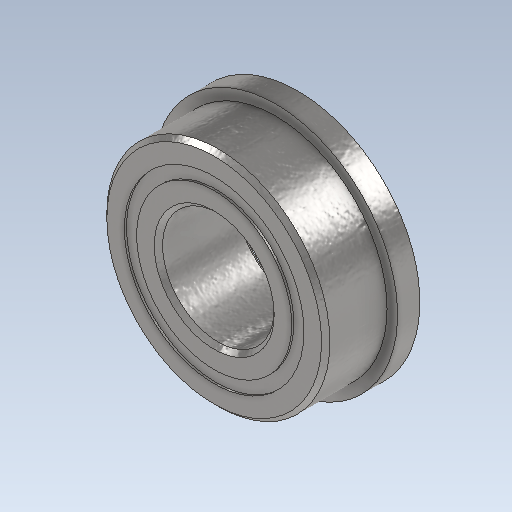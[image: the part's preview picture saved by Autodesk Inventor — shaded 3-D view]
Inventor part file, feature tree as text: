
AUTODESK INVENTOR PART (.ipt)
format: ipt  version: 2023 (Build 270158000, 158)  size: 664,576 bytes
history: native  units: in
note: dims shown in document units (in); Inventor stores cm internally (conversion verified against a paired STEP export)
features: other x11, revolve x5
ambient origin geometry x8: Origin, YZ Plane, XZ Plane, XY Plane, X Axis, Y Axis, Z Axis, Center Point
bodies: Solid1 (feature_tree), Solid2 (feature_tree), Solid3 (feature_tree), Solid4 (feature_tree), Solid5 (feature_tree), Solid6 (feature_tree), Solid7 (feature_tree), Solid8 (feature_tree), Solid9 (feature_tree), Solid10 (feature_tree), Solid11 (feature_tree), Solid12 (feature_tree), Solid13 (feature_tree), Solid14 (feature_tree), Solid15 (feature_tree), Solid16 (feature_tree)
feature tree (16):
  revolve  "Revolve3"  [1 undecoded]
  revolve  "Revolve4"  [1 undecoded]
  other  "CirPattern1[1]"
  other  "CirPattern1[2]"
  other  "CirPattern1[3]"
  other  "CirPattern1[4]"
  other  "CirPattern1[5]"
  other  "CirPattern1[6]"
  other  "CirPattern1[7]"
  other  "CirPattern1[8]"
  other  "CirPattern1[9]"
  other  "CirPattern1[10]"
  other  "CirPattern1[11]"
  revolve  "Revolve5[1]"  [1 undecoded]
  revolve  "Revolve5[2]"  [1 undecoded]
  revolve  "Revolve6"  [1 undecoded]
note: 5 required parameter values undecoded (feature->parameter linkage not recoverable at this tier; creation-order binding heuristic only, values carry confidence <= 0.55)
